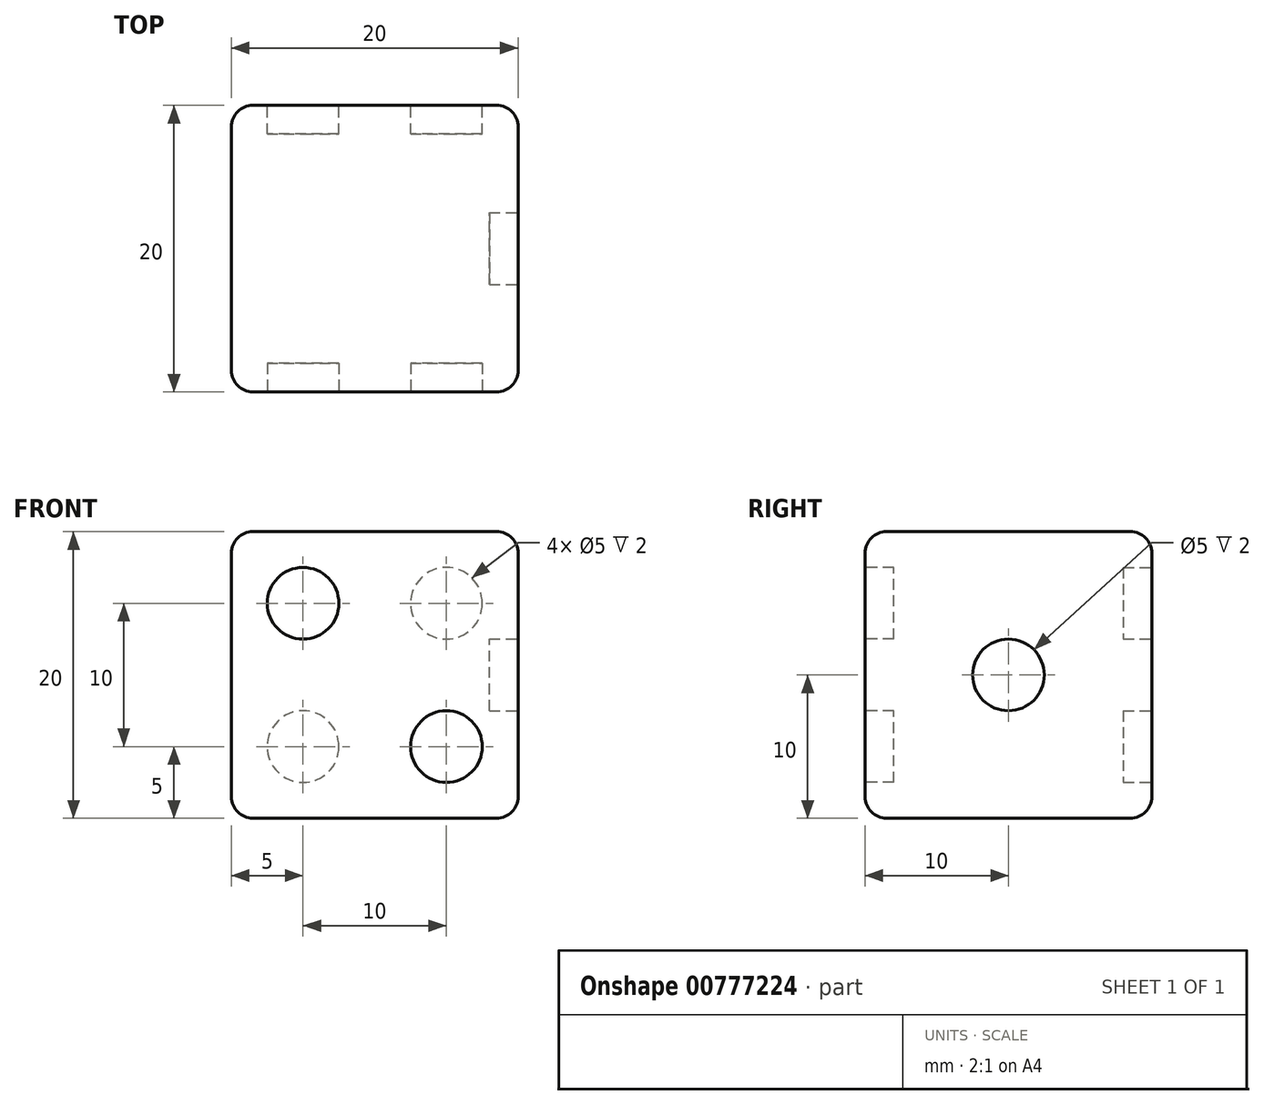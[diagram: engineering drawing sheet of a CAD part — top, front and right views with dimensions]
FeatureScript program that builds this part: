
annotation { "Feature Type Name" : "Feature", "Feature Type Description" : "" }
export const myFeature = defineFeature(function(context is Context, id is Id, definition is map)
    precondition{}
    {
        {
            var Q0;
            Q0=qCreatedBy(makeId("Top.planeOp"),FACE);
            var sketch = newSketch(context, id + "F0", { "sketchPlane" : qUnion([Q0])});
            skLineSegment(sketch, "E0.bottom", {"start": v(-10, 10) * mm, "end": v(10, 10) * mm});
            skLineSegment(sketch, "E0.top", {"start": v(-10, -10) * mm, "end": v(10, -10) * mm});
            skLineSegment(sketch, "E0.left", {"start": v(-10, 10) * mm, "end": v(-10, -10) * mm});
            skLineSegment(sketch, "E0.right", {"start": v(10, 10) * mm, "end": v(10, -10) * mm});
            skPoint(sketch, "E0.middle", {"position": v(0, 0) * mm});
            skSolve(sketch);
        }
        {
            var Q0;
            Q0 = qSketchRegion(id + "F0", true);
            extrude(context, id + "F1", {"entities" : qUnion([Q0]), "endBound" : BoundingType.SYMMETRIC, "depth" : 20 * mm, "offsetDistance" : 25 * mm});
        }
        {
            var Q0;
            Q0=makeQuery(id+"F1.opExtrude","SWEPT_FACE",FACE,{"disambiguationData":[OSD([sQuery(id+"F0.wireOp",EDGE,"E0.right")])]});
            var sketch = newSketch(context, id + "F2", { "sketchPlane" : qUnion([Q0])});
            skCircle(sketch, "E1", {"center": v(0, 0) * mm, "radius": 2.5 * mm});
            skLineSegment(sketch, "E2", {"start": v(0, 0) * mm, "end": v(0, 3.4) * mm, "construction": true});
            skSolve(sketch);
        }
        {
            var Q0;
            Q0 = qSketchRegion(id + "F2", true);
            extrude(context, id + "F3", {"entities" : qUnion([Q0]), "operationType" : NewBodyOperationType.REMOVE, "oppositeDirection" : true, "depth" : 2 * mm, "offsetDistance" : 25 * mm});
        }
        {
            var Q0;
            Q0=makeQuery(id+"F1.opExtrude","SWEPT_FACE",FACE,{"disambiguationData":[OSD([sQuery(id+"F0.wireOp",EDGE,"E0.bottom")])]});
            var sketch = newSketch(context, id + "F4", { "sketchPlane" : qUnion([Q0])});
            skCircle(sketch, "E3", {"center": v(-5, 5) * mm, "radius": 2.5 * mm});
            skCircle(sketch, "E4", {"center": v(5, -5) * mm, "radius": 2.5 * mm});
            skSolve(sketch);
        }
        {
            var Q0;
            Q0=makeQuery(id+"F4.imprint","IMPRINT",FACE,{"disambiguationData":[TD([[makeQuery(id+"F4.imprint","IMPRINT",EDGE,{"derivedFrom":sQuery(id+"F4.wireOp",EDGE,"E4")}),1.0]])]});
            var Q1;
            Q1=makeQuery(id+"F4.imprint","IMPRINT",FACE,{"disambiguationData":[TD([[makeQuery(id+"F4.imprint","IMPRINT",EDGE,{"derivedFrom":sQuery(id+"F4.wireOp",EDGE,"E3")}),1.0]])]});
            var Q2;
            Q2=sQuery(id+"F4.wireOp",EDGE,"E3");
            var Q3;
            Q3=sQuery(id+"F4.wireOp",EDGE,"E4");
            extrude(context, id + "F5", {"entities" : qUnion([Q0, Q1]), "operationType" : NewBodyOperationType.REMOVE, "surfaceEntities" : qUnion([Q2, Q3]), "oppositeDirection" : true, "depth" : 2 * mm, "offsetDistance" : 25 * mm});
        }
        {
            var Q0;
            Q0=makeQuery(id+"F1.opExtrude","SWEPT_FACE",FACE,{"disambiguationData":[OSD([sQuery(id+"F0.wireOp",EDGE,"E0.top")])]});
            var sketch = newSketch(context, id + "F6", { "sketchPlane" : qUnion([Q0])});
            skCircle(sketch, "E5", {"center": v(-5, 5) * mm, "radius": 2.5 * mm});
            skCircle(sketch, "E6", {"center": v(5, -5) * mm, "radius": 2.5 * mm});
            skSolve(sketch);
        }
        {
            var Q0;
            Q0 = qSketchRegion(id + "F6", true);
            extrude(context, id + "F7", {"entities" : qUnion([Q0]), "operationType" : NewBodyOperationType.REMOVE, "oppositeDirection" : true, "depth" : 2 * mm, "offsetDistance" : 25 * mm});
        }
        {
            var Q0;
            Q0=makeQuery(id+"F1.opExtrude","CAP_EDGE",EDGE,{"disambiguationData":[OSD([sQuery(id+"F0.wireOp",EDGE,"E0.right")])],"isStart":false});
            var Q1;
            Q1=makeQuery(id+"F1.opExtrude","CAP_EDGE",EDGE,{"disambiguationData":[OSD([sQuery(id+"F0.wireOp",EDGE,"E0.bottom")])],"isStart":false});
            var Q2;
            Q2=makeQuery(id+"F1.opExtrude","SWEPT_EDGE",EDGE,{"disambiguationData":[OSD([sQuery(id+"F0.wireOp",EDGE,"E0.bottom"),sQuery(id+"F0.wireOp",EDGE,"E0.right")])]});
            var Q3;
            Q3=makeQuery(id+"F1.opExtrude","SWEPT_EDGE",EDGE,{"disambiguationData":[OSD([sQuery(id+"F0.wireOp",EDGE,"E0.top"),sQuery(id+"F0.wireOp",EDGE,"E0.right")])]});
            var Q4;
            Q4=makeQuery(id+"F1.opExtrude","CAP_EDGE",EDGE,{"disambiguationData":[OSD([sQuery(id+"F0.wireOp",EDGE,"E0.right")])],"isStart":true});
            var Q5;
            Q5=makeQuery(id+"F1.opExtrude","CAP_EDGE",EDGE,{"disambiguationData":[OSD([sQuery(id+"F0.wireOp",EDGE,"E0.top")])],"isStart":true});
            var Q6;
            Q6=makeQuery(id+"F1.opExtrude","CAP_EDGE",EDGE,{"disambiguationData":[OSD([sQuery(id+"F0.wireOp",EDGE,"E0.left")])],"isStart":true});
            var Q7;
            Q7=makeQuery(id+"F1.opExtrude","CAP_EDGE",EDGE,{"disambiguationData":[OSD([sQuery(id+"F0.wireOp",EDGE,"E0.bottom")])],"isStart":true});
            var Q8;
            Q8=makeQuery(id+"F1.opExtrude","SWEPT_EDGE",EDGE,{"disambiguationData":[OSD([sQuery(id+"F0.wireOp",EDGE,"E0.bottom"),sQuery(id+"F0.wireOp",EDGE,"E0.left")])]});
            var Q9;
            Q9=makeQuery(id+"F1.opExtrude","SWEPT_EDGE",EDGE,{"disambiguationData":[OSD([sQuery(id+"F0.wireOp",EDGE,"E0.top"),sQuery(id+"F0.wireOp",EDGE,"E0.left")])]});
            var Q10;
            Q10=makeQuery(id+"F1.opExtrude","CAP_EDGE",EDGE,{"disambiguationData":[OSD([sQuery(id+"F0.wireOp",EDGE,"E0.top")])],"isStart":false});
            var Q11;
            Q11=makeQuery(id+"F1.opExtrude","CAP_EDGE",EDGE,{"disambiguationData":[OSD([sQuery(id+"F0.wireOp",EDGE,"E0.left")])],"isStart":false});
            fillet(context, id + "F8", {"entities" : qUnion([Q0, Q1, Q2, Q3, Q4, Q5, Q6, Q7, Q8, Q9, Q10, Q11]), "radius" : 1.5 * mm, "tangentPropagation" : true, "allowEdgeOverflow" : false});
        }
    });
